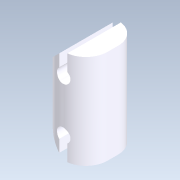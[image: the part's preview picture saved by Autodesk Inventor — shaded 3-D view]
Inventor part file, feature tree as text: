
AUTODESK INVENTOR PART (.ipt)
format: ipt  version: 2020.2 (Build 242310000, 310)  size: 166,400 bytes
history: native  units: mm
features: extrude x3, sketch x3, fillet x1
ambient origin geometry x8: Origin, YZ Plane, XZ Plane, XY Plane, X Axis, Y Axis, Z Axis, Center Point
bodies: Solid1 (feature_tree)
feature tree (7):
  extrude  "Extrusion1"  Depth=35.0mm
  extrude  "Extrusion2"  Depth=17.0mm
  fillet  "Fillet1"  Radius=17.0mm
  extrude  "Extrusion4"  TaperAngle=0.0deg  [1 undecoded]
  sketch  "Sketch1"  dims[d1=2.5mm d2=35.0mm]
  sketch  "Sketch2"  dims[d3=5.0mm d5=17.0mm d9=17.0mm]
  sketch  "Sketch4"  dims[d10=2.5mm d11=0.0mm d12=135.0deg d13=135.0deg d14=20.0mm d15=0.0mm d16=8.0mm d17=5.0mm d18=1.5mm d19=3.0mm d20=8.0mm d21=1.5mm d22=1.5mm d23=5.0mm d24=0.0mm d25=0.0mm d26=8.0mm d31=2.0mm d32=2.0mm d33=0.0mm d34=0.0mm]
note: 1 required parameter value undecoded (feature->parameter linkage not recoverable at this tier; creation-order binding heuristic only, values carry confidence <= 0.55)
